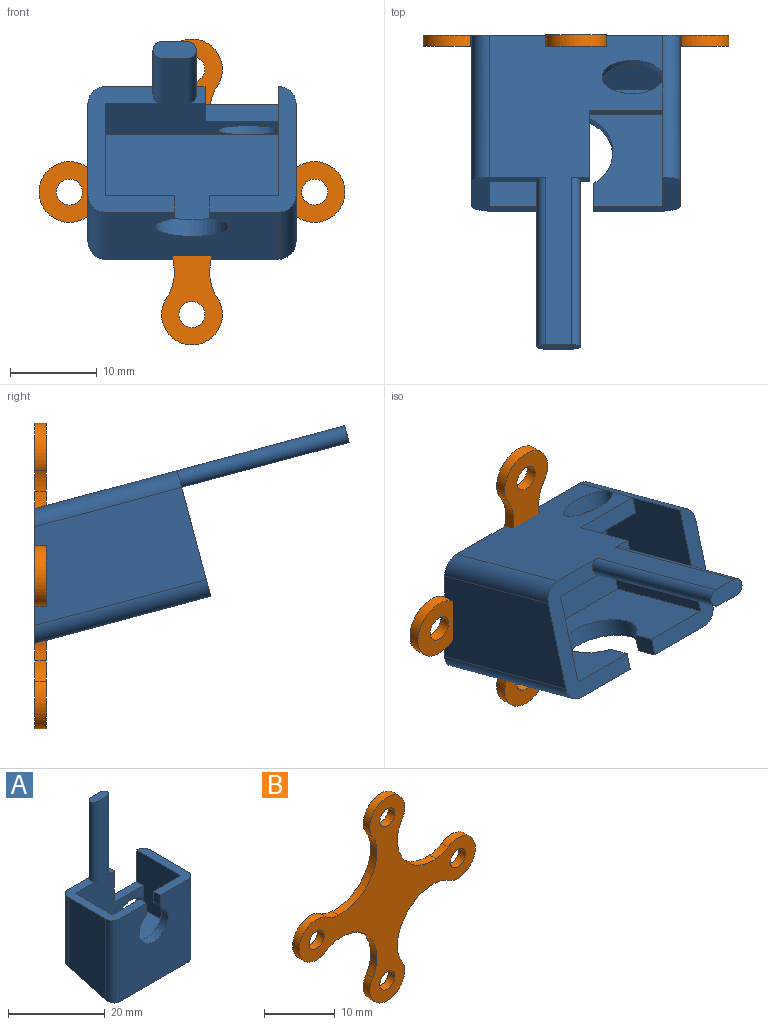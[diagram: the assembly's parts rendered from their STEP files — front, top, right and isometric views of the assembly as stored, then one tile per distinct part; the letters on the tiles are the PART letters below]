
ASSEMBLY  parts=2 mates=1
PART A: 26 faces, bbox 24x15x41 mm
  f0: plane 36.98x20mm, normal (0,1,0), area 309.6mm2, adj f2,f5,f15,f16,f17,f18,f19,f20
  f1: plane 20.46x11mm, normal (-1,0,0), area 208.9mm2, adj f5,f20,f22,f23
  f2: plane 2x2mm, normal (0,0,1), area 2.4mm2, adj f0,f3,f16,f18
  f3: plane 34x20mm, normal (0,-1,0), area 250mm2, adj f2,f5,f8,f9,f11,f15,f16,f17
  f4: plane 15x10mm, normal (0,0,1), area 44.3mm2, adj f6,f7,f8,f10,f13,f21,f24
  f5: plane 15x10mm, normal (0,0,1), area 55.7mm2, adj f0,f1,f3,f7,f9,f10,f14,f17
  f6: plane 20.46x11mm, normal (1,0,0), area 208.9mm2, adj f4,f20,f21,f24
  f7: plane 21x20mm, normal (0,-1,0), area 353.6mm2, adj f4,f5,f12,f13,f14,f20,f23,f24
  f8: plane 14x13mm, normal (-1,0,0), area 170mm2, adj f3,f4,f10,f11,f19,f21
  f9: plane 14x11mm, normal (1,0,0), area 154mm2, adj f3,f5,f10,f11
  f10: plane 20x14mm, normal (0,1,0), area 213.6mm2, adj f4,f5,f8,f9,f11,f12,f13,f14
  f11: plane 20x11mm, normal (0,0,1), area 220mm2, adj f3,f8,f9,f10
  f12: cylinder r=4.25mm len=8.5mm, axis (0,-1,0), area 45.1mm2, adj f7,f10,f13,f14
  f13: plane 2.75x2mm, normal (-1,0,0), area 5.5mm2, adj f4,f7,f10,f12
  f14: plane 2.75x2mm, normal (1,0,0), area 5.5mm2, adj f5,f7,f10,f12
  f15: plane 5x2mm, normal (0,0,1), area 9.1mm2, adj f0,f3,f16,f17
  f16: cylinder r=1mm len=20mm, axis (0,0,-1), area 62.8mm2, adj f0,f2,f3,f15
  f17: cylinder r=1mm len=20mm, axis (0,0,1), area 62.8mm2, adj f0,f3,f5,f15
  f18: plane 8x2mm, normal (1,0,0), area 16mm2, adj f0,f2,f3,f19
  f19: plane 8.5x2mm, normal (0,0,1), area 17mm2, adj f0,f3,f8,f18
  f20: plane 24x15mm, normal (0,0.26,-0.97), area 369.1mm2, adj f0,f1,f6,f7,f21,f22,f23,f24
  f21: cylinder r=2mm len=17.52mm, axis (0,0,-1), area 54mm2, adj f0,f4,f6,f8,f20
  f22: cylinder r=2mm len=17.52mm, axis (0,0,1), area 54mm2, adj f0,f1,f5,f20
  f23: cylinder r=2mm len=21mm, axis (0,0,-1), area 65.4mm2, adj f1,f5,f7,f20
  f24: cylinder r=2mm len=21mm, axis (0,0,1), area 65.4mm2, adj f4,f6,f7,f20
  f25: extruded ~7x4mm, area 35.2mm2, adj f0,f3
PART B: 22 faces, bbox 35.3x1.3x35.3 mm
  f0: cylinder r=5mm len=2.39mm, axis (0,1,0), area 3.3mm2, adj f1,f19,f20,f21
  f1: cylinder r=3.5mm len=7mm, axis (0,1,0), area 19.7mm2, adj f0,f2,f20,f21
  f2: cylinder r=5mm len=2.39mm, axis (0,1,0), area 3.3mm2, adj f1,f3,f20,f21
  f3: cylinder r=7.18mm len=7.75mm, axis (0,1,0), area 16.1mm2, adj f2,f4,f20,f21
  f4: cylinder r=5mm len=2.39mm, axis (0,1,0), area 3.3mm2, adj f3,f5,f20,f21
  f5: cylinder r=3.5mm len=7mm, axis (0,1,0), area 19.7mm2, adj f4,f6,f20,f21
  f6: cylinder r=5mm len=2.39mm, axis (0,1,0), area 3.3mm2, adj f5,f7,f20,f21
  f7: cylinder r=7.18mm len=7.75mm, axis (0,1,0), area 16.1mm2, adj f6,f8,f20,f21
  f8: cylinder r=5mm len=2.39mm, axis (0,1,0), area 3.3mm2, adj f7,f9,f20,f21
  f9: cylinder r=3.5mm len=7mm, axis (0,1,0), area 19.7mm2, adj f8,f10,f20,f21
  f10: cylinder r=5mm len=2.39mm, axis (0,1,0), area 3.3mm2, adj f9,f11,f20,f21
  f11: cylinder r=7.18mm len=7.75mm, axis (0,1,0), area 16.1mm2, adj f10,f12,f20,f21
  f12: cylinder r=5mm len=2.39mm, axis (0,1,0), area 3.3mm2, adj f11,f13,f20,f21
  f13: cylinder r=3.5mm len=7mm, axis (0,1,0), area 19.7mm2, adj f12,f14,f20,f21
  f14: cylinder r=5mm len=2.39mm, axis (0,1,0), area 3.3mm2, adj f13,f19,f20,f21
  f15: cylinder r=1.5mm len=3mm, axis (0,1,0), area 12.3mm2, adj f20,f21
  f16: cylinder r=1.5mm len=3mm, axis (0,1,0), area 12.3mm2, adj f20,f21
  f17: cylinder r=1.5mm len=3mm, axis (0,1,0), area 12.3mm2, adj f20,f21
  f18: cylinder r=1.5mm len=3mm, axis (0,1,0), area 12.3mm2, adj f20,f21
  f19: cylinder r=7.18mm len=7.75mm, axis (0,1,0), area 16.1mm2, adj f0,f14,f20,f21
  f20: plane 35.28x35.28mm, normal (0,-1,0), area 333.8mm2, adj f0,f1,f2,f3,f4,f5,f6,f7
  f21: plane 35.28x35.28mm, normal (0,1,0), area 333.8mm2, adj f0,f1,f2,f3,f4,f5,f6,f7
PLACE A rot(axis=(1,0,0),75deg) t=(0,-41.69,0.77)mm
PLACE B t=(0,-38.8,0)mm
MATE planar A.f20 <-> B.f21  axis (0,1,0) through (0,-38.8,0)mm
